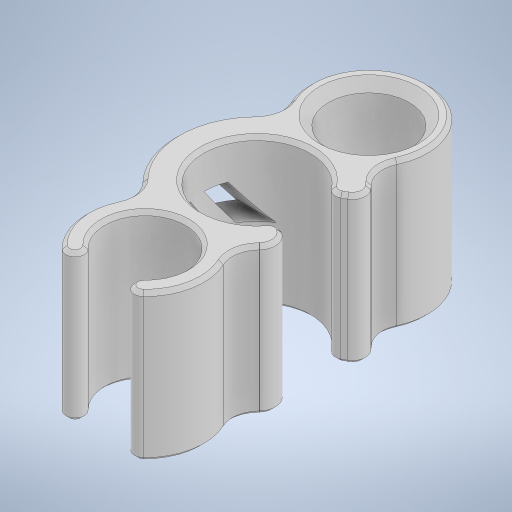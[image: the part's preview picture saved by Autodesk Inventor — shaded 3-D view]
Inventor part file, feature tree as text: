
AUTODESK INVENTOR PART (.ipt)
format: ipt  version: 2024.2 (Build 282272000, 272)  size: 390,144 bytes
history: native  units: mm
features: fillet x5, extrude x2, chamfer x2, sketch x2, plane x1
ambient origin geometry x8: Origin, YZ Plane, XZ Plane, XY Plane, X Axis, Y Axis, Z Axis, Center Point
bodies: Solid1 (feature_tree)
feature tree (12):
  extrude  "Extrusion1"  Depth=4.4mm
  fillet  "Fillet1"  Radius=4.4mm
  fillet  "Fillet2"  Radius=6.1mm
  fillet  "Fillet3"  Radius=6.1mm
  fillet  "Fillet4"  Radius=1.5mm
  fillet  "Fillet5"  Radius=1.0mm
  plane  "Work Plane1"
  extrude  "Extrusion2"  Depth=8.0mm TaperAngle=0.0deg
  chamfer  "Chamfer1"  Distance=2.8mm
  chamfer  "Chamfer2"  Distance=1.4mm
  sketch  "Sketch1"  dims[d0=5.8mm d1=4.4mm d2=4.4mm d3=6.1mm d4=6.1mm d5=1.5mm d6=1.0mm]
  sketch  "Sketch2"  dims[d7=1.0mm d8=8.0mm d9=0.0mm d10=2.8mm d11=1.4mm d12=1.5mm d13=2.4mm d14=1.2mm d15=0.9mm d16=0.5mm d17=0.7mm d18=0.5mm d19=21.816616mm d20=4.0mm d21=5.0mm d22=0.85mm d23=2.5mm d24=2.0mm d26=8.0mm d27=0.0mm d28=0.5mm d29=2.0mm d30=45.0deg d31=0.2mm d32=2.0mm d33=45.0deg]
